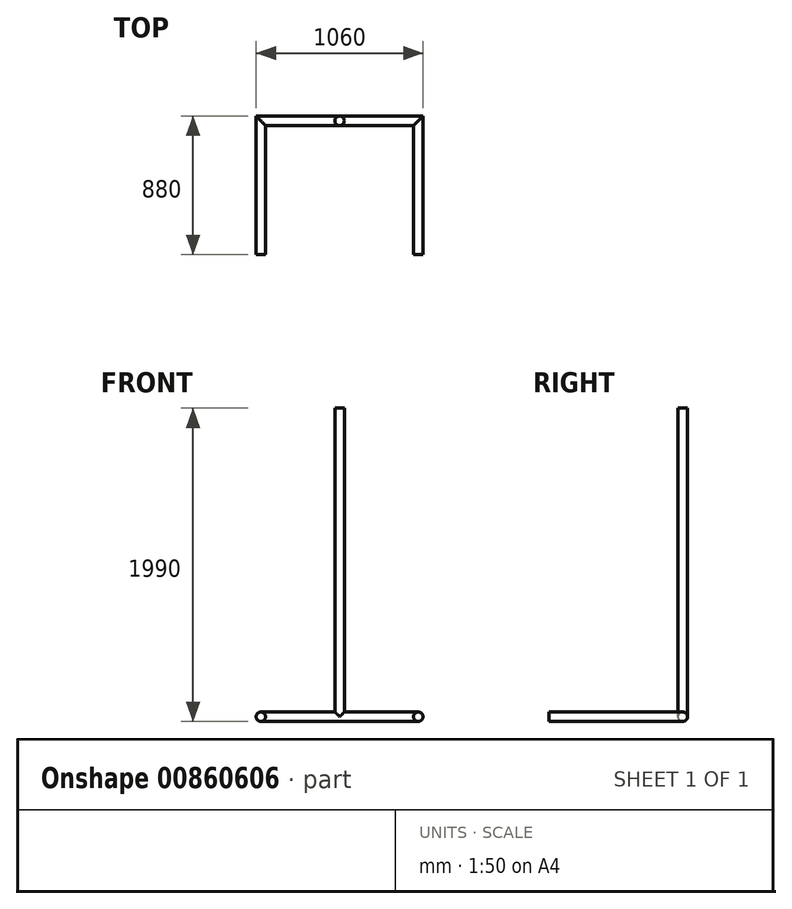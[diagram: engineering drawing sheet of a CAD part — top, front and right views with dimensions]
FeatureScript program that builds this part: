
annotation { "Feature Type Name" : "Feature", "Feature Type Description" : "" }
export const myFeature = defineFeature(function(context is Context, id is Id, definition is map)
    precondition{}
    {
        {
            var Q0;
            Q0=qCreatedBy(makeId("Top.planeOp"),FACE);
            var sketch = newSketch(context, id + "F0", { "sketchPlane" : qUnion([Q0])});
            skLineSegment(sketch, "E0", {"start": v(-500, -510.78) * mm, "end": v(-500, 339.22) * mm});
            skLineSegment(sketch, "E1", {"start": v(-500, 339.22) * mm, "end": v(500, 339.22) * mm});
            skLineSegment(sketch, "E2", {"start": v(500, 339.22) * mm, "end": v(500, -510.78) * mm});
            skLineSegment(sketch, "E3", {"start": v(0, 339.22) * mm, "end": v(0, -475.25) * mm, "construction": true});
            skLineSegment(sketch, "E4", {"start": v(-506.24, 0) * mm, "end": v(599.73, 0) * mm, "construction": true});
            skSolve(sketch);
        }
        {
            var Q0;
            Q0=qCreatedBy(makeId("Front.planeOp"),FACE);
            var Q1;
            Q1=sQuery(id+"F0.wireOp",VERTEX,"E0.start");
            cPlane(context, id + "F1", {"entities" : qUnion([Q0, Q1]), "cplaneType" : CPlaneType.PLANE_POINT, "offset" : 25.4 * mm, "width" : 152.4 * mm, "height" : 152.4 * mm});
        }
        {
            var Q0;
            Q0=qCreatedBy(id+"F1.planeOp",FACE);
            var sketch = newSketch(context, id + "F2", { "sketchPlane" : qUnion([Q0])});
            skCircle(sketch, "E5", {"center": v(-500, 0) * mm, "radius": 30 * mm});
            skSolve(sketch);
        }
        {
            var Q0;
            Q0=qCreatedBy(makeId("Top.planeOp"),FACE);
            var Q1;
            Q1=sQuery(id+"F0.wireOp",VERTEX,"E3.start");
            cPlane(context, id + "F3", {"entities" : qUnion([Q0, Q1]), "cplaneType" : CPlaneType.PLANE_POINT, "offset" : 25.4 * mm, "width" : 152.4 * mm, "height" : 152.4 * mm});
        }
        {
            var Q0;
            Q0=qCreatedBy(id+"F3.planeOp",FACE);
            var sketch = newSketch(context, id + "F4", { "sketchPlane" : qUnion([Q0])});
            skCircle(sketch, "E6", {"center": v(0, 339.22) * mm, "radius": 30 * mm});
            skSolve(sketch);
        }
        {
            var Q0;
            Q0=makeQuery(id+"F2.imprint","IMPRINT",FACE,{"disambiguationData":[TD([[makeQuery(id+"F2.imprint","IMPRINT",EDGE,{"derivedFrom":sQuery(id+"F2.wireOp",EDGE,"E5")}),1.0]])]});
            var Q1;
            Q1=sQuery(id+"F0.wireOp",EDGE,"E0");
            var Q2;
            Q2=sQuery(id+"F0.wireOp",EDGE,"E1");
            var Q3;
            Q3=sQuery(id+"F0.wireOp",EDGE,"E2");
            sweep(context, id + "F5", {"profiles" : qUnion([Q0]), "path" : qUnion([Q1, Q2, Q3])});
        }
        {
            var Q0;
            Q0=qCreatedBy(makeId("Front.planeOp"),FACE);
            var Q1;
            Q1=sQuery(id+"F4.wireOp",VERTEX,"E6.center");
            cPlane(context, id + "F6", {"entities" : qUnion([Q0, Q1]), "cplaneType" : CPlaneType.PLANE_POINT, "offset" : 25.4 * mm, "width" : 152.4 * mm, "height" : 152.4 * mm});
        }
        {
            var Q0;
            Q0=qCreatedBy(id+"F6.planeOp",FACE);
            var sketch = newSketch(context, id + "F7", { "sketchPlane" : qUnion([Q0])});
            skLineSegment(sketch, "E7", {"start": v(0, 0) * mm, "end": v(0, 1960) * mm});
            skSolve(sketch);
        }
        {
            var Q0;
            Q0 = qSketchRegion(id + "F4", true);
            var Q1;
            Q1=sQuery(id+"F7.wireOp",EDGE,"E7");
            sweep(context, id + "F8", {"operationType" : NewBodyOperationType.ADD, "profiles" : qUnion([Q0]), "path" : qUnion([Q1])});
        }
    });
